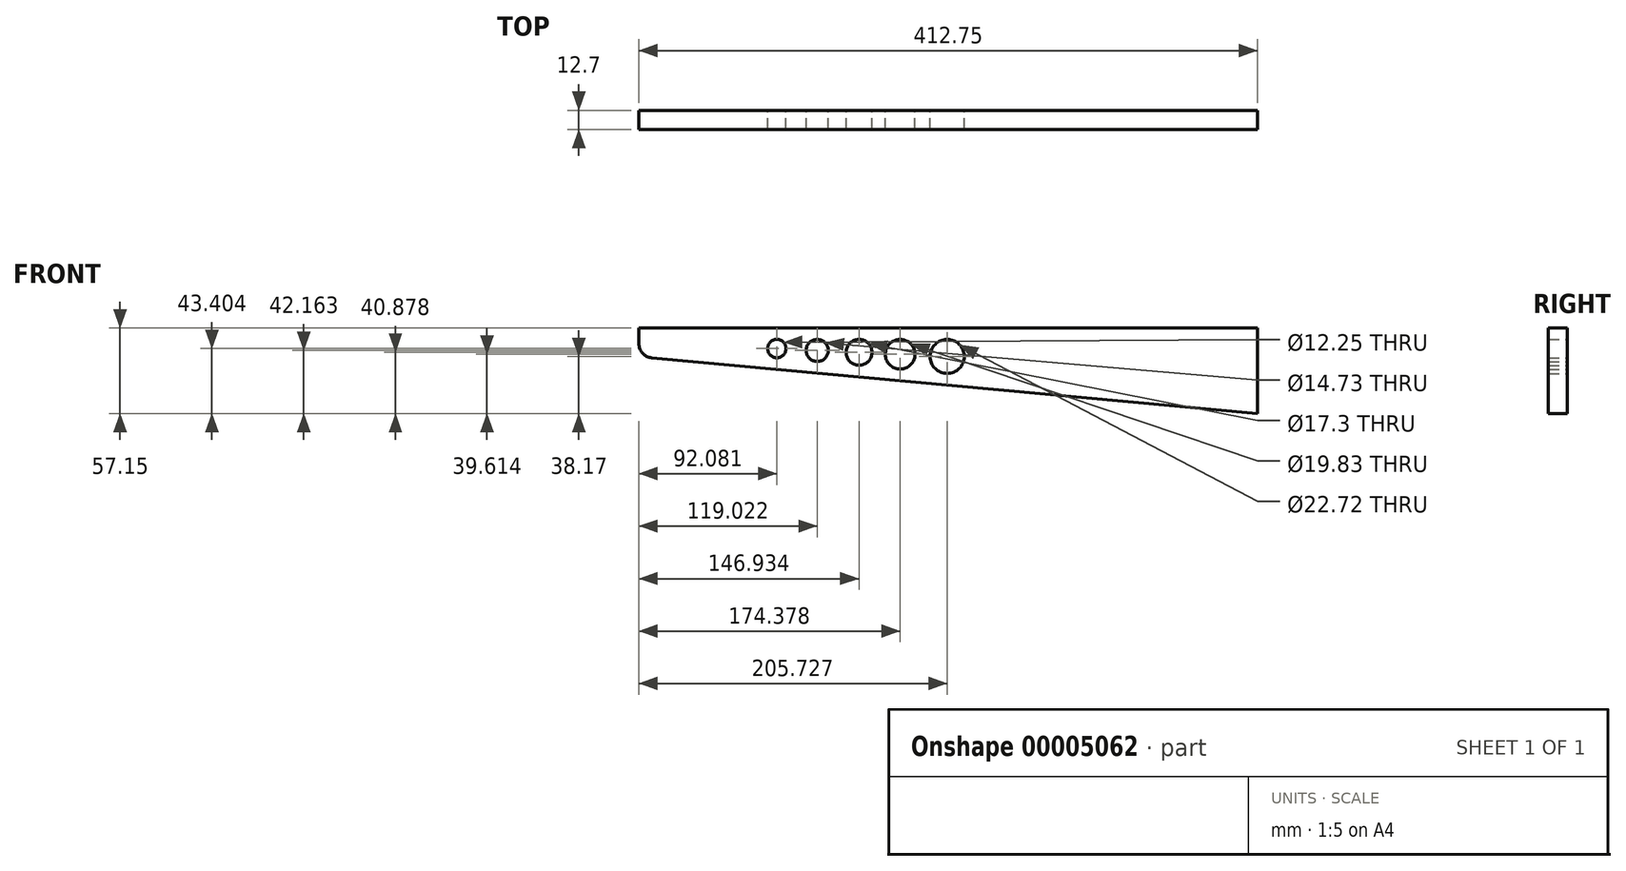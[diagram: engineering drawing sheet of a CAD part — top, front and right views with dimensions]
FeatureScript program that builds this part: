
annotation { "Feature Type Name" : "Feature", "Feature Type Description" : "" }
export const myFeature = defineFeature(function(context is Context, id is Id, definition is map)
    precondition{}
    {
        {
            var Q0;
            Q0=qCreatedBy(makeId("Front.planeOp"),FACE);
            var sketch = newSketch(context, id + "F0", { "sketchPlane" : qUnion([Q0])});
            skLineSegment(sketch, "E0", {"start": v(0, 0) * mm, "end": v(-412.75, 0) * mm});
            skLineSegment(sketch, "E1", {"start": v(-412.75, 0) * mm, "end": v(-412.75, -10.36) * mm});
            skLineSegment(sketch, "E2", {"start": v(-404.1, -19.85) * mm, "end": v(0, -57.15) * mm});
            skLineSegment(sketch, "E3", {"start": v(0, -57.15) * mm, "end": v(0, 0) * mm});
            skPoint(sketch, "E4.visualSharp", {"position": v(-412.75, -19.05) * mm});
            skArc(sketch, "E4.filletArc", {"start": v(-412.75, -10.36) * mm, "mid": v(-410.26, -16.78) * mm, "end": v(-404.1, -19.85) * mm});
            skLineSegment(sketch, "E5", {"start": v(10.5, -7.62) * mm, "end": v(-453.67, -7.62) * mm, "construction": true});
            skLineSegment(sketch, "E6", {"start": v(34.08, -52.64) * mm, "end": v(-453.67, -7.62) * mm, "construction": true});
            skCircle(sketch, "E7", {"center": v(-320.67, -13.75) * mm, "radius": 6.13 * mm});
            skCircle(sketch, "E8", {"center": v(-293.73, -14.99) * mm, "radius": 7.37 * mm});
            skCircle(sketch, "E9", {"center": v(-265.82, -16.27) * mm, "radius": 8.65 * mm});
            skCircle(sketch, "E10", {"center": v(-238.37, -17.54) * mm, "radius": 9.92 * mm});
            skCircle(sketch, "E11", {"center": v(-207.02, -18.98) * mm, "radius": 11.36 * mm});
            skSolve(sketch);
        }
        {
            var Q0;
            Q0 = qSketchRegion(id + "F0", true);
            extrude(context, id + "F1", {"entities" : qUnion([Q0]), "depth" : 12.7 * mm});
        }
    });
